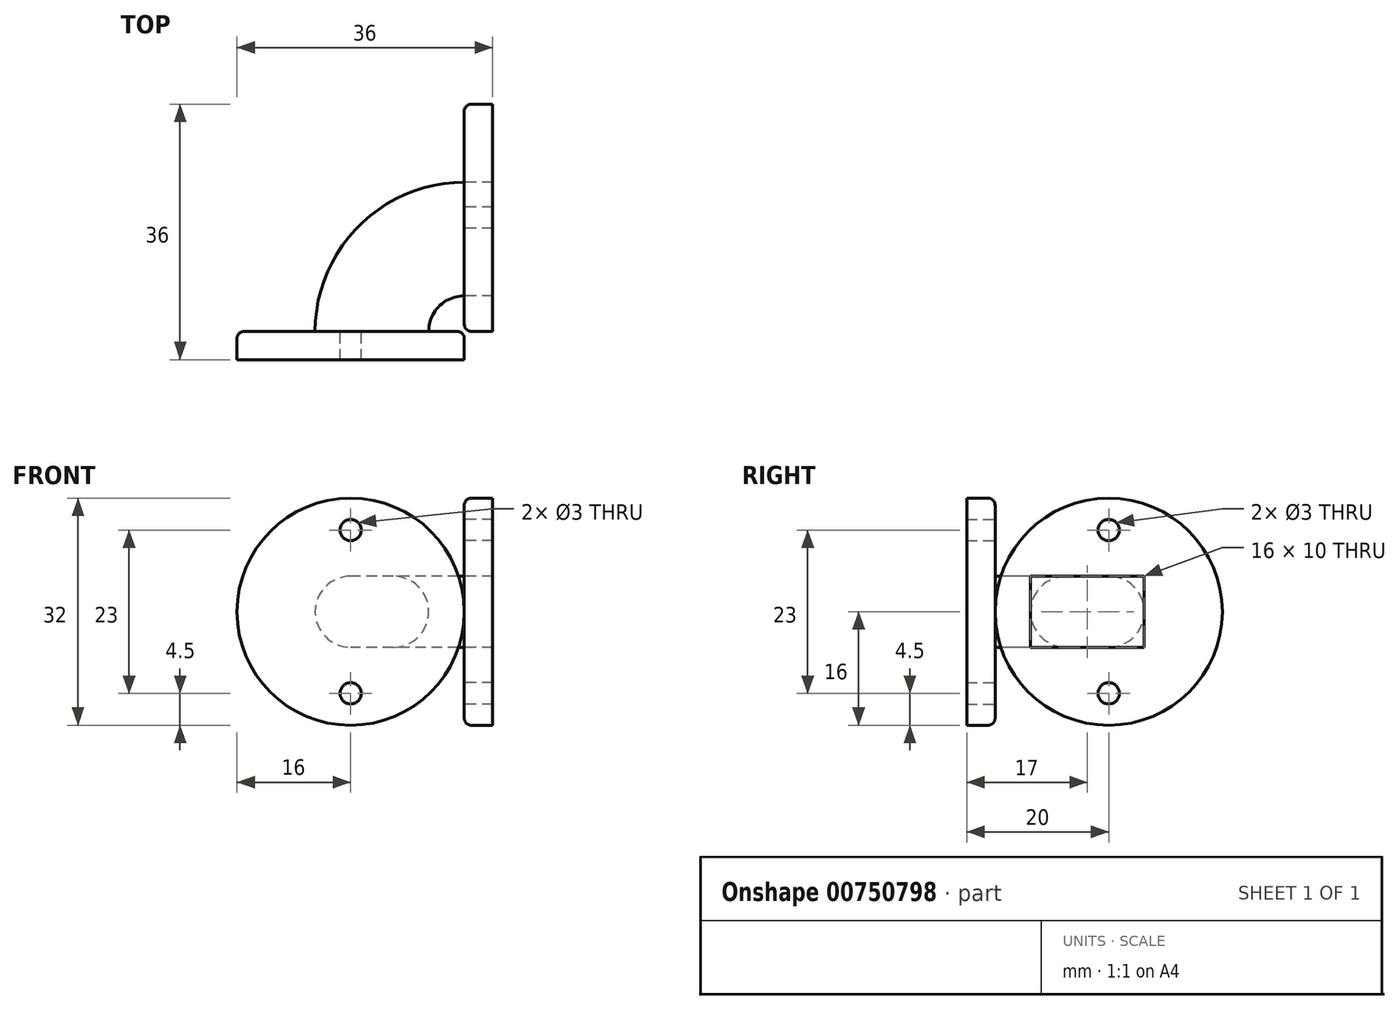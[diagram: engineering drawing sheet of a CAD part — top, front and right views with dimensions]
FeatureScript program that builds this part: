
annotation { "Feature Type Name" : "Feature", "Feature Type Description" : "" }
export const myFeature = defineFeature(function(context is Context, id is Id, definition is map)
    precondition{}
    {
        {
            var Q0;
            Q0=qCreatedBy(makeId("Front.planeOp"),FACE);
            var sketch = newSketch(context, id + "F0", { "sketchPlane" : qUnion([Q0])});
            skCircle(sketch, "E0", {"center": v(0, 0) * mm, "radius": 16 * mm});
            skCircle(sketch, "E1", {"center": v(0, -11.5) * mm, "radius": 1.5 * mm});
            skCircle(sketch, "E2", {"center": v(0, 11.5) * mm, "radius": 1.5 * mm});
            skSolve(sketch);
        }
        {
            var Q0;
            Q0=makeQuery(id+"F0.imprint","IMPRINT",FACE,{"disambiguationData":[TD([[makeQuery(id+"F0.imprint","IMPRINT",EDGE,{"derivedFrom":sQuery(id+"F0.wireOp",EDGE,"E0")}),1.0]])]});
            extrude(context, id + "F1", {"entities" : qUnion([Q0]), "depth" : 4 * mm, "offsetDistance" : 25 * mm});
        }
        {
            var Q0;
            Q0=qCreatedBy(makeId("Top.planeOp"),FACE);
            var sketch = newSketch(context, id + "F2", { "sketchPlane" : qUnion([Q0])});
            skCircle(sketch, "E3", {"center": v(16, 0) * mm, "radius": 16 * mm});
            skLineSegment(sketch, "E4", {"start": v(0, 0) * mm, "end": v(16, 0) * mm});
            skLineSegment(sketch, "E5", {"start": v(16, 0) * mm, "end": v(16, 16) * mm});
            skCircle(sketch, "E6", {"center": v(16, 0) * mm, "radius": 5 * mm});
            skCircle(sketch, "E7", {"center": v(16, 0) * mm, "radius": 21 * mm});
            skLineSegment(sketch, "E8", {"start": v(16, 16) * mm, "end": v(16, 21) * mm});
            skLineSegment(sketch, "E9", {"start": v(0, 0) * mm, "end": v(-5, 0) * mm});
            skSolve(sketch);
        }
        {
            var Q0;
            {var subQ2=sQuery(id+"F2.wireOp",EDGE,"E8");Q0=makeQuery(id+"F2.imprint","IMPRINT",FACE,{"disambiguationData":[TD([[makeQuery(id+"F2.imprint","IMPRINT",EDGE,{"derivedFrom":subQ2}),1.0]])]});}
            var Q1;
            {var subQ0=sQuery(id+"F2.wireOp",EDGE,"E4");var subQ5=sQuery(id+"F2.wireOp",EDGE,"E6");var subQ7=makeQuery(id+"F2.imprint","INTERSECT",VERTEX,{"derivedFrom":[subQ0,subQ5]});Q1=makeQuery(id+"F2.imprint","IMPRINT",FACE,{"disambiguationData":[TD([[makeQuery(id+"F2.imprint","IMPRINT",EDGE,{"disambiguationData":[TD([[subQ7,1.0]])],"derivedFrom":subQ5}),-1.0]])]});}
            extrude(context, id + "F3", {"entities" : qUnion([Q0, Q1]), "operationType" : NewBodyOperationType.ADD, "endBound" : BoundingType.SYMMETRIC, "depth" : 10 * mm, "offsetDistance" : 25 * mm});
        }
        {
            var Q0;
            Q0=makeQuery(id+"F3.opExtrude","SWEPT_FACE",FACE,{"disambiguationData":[OSD([sQuery(id+"F2.wireOp",EDGE,"E5"),sQuery(id+"F2.wireOp",EDGE,"E8")])]});
            var sketch = newSketch(context, id + "F4", { "sketchPlane" : qUnion([Q0])});
            skCircle(sketch, "E10", {"center": v(16, 0) * mm, "radius": 16 * mm});
            skCircle(sketch, "E11", {"center": v(16, -11.5) * mm, "radius": 1.5 * mm});
            skCircle(sketch, "E12", {"center": v(16, 11.5) * mm, "radius": 1.5 * mm});
            skSolve(sketch);
        }
        {
            var Q0;
            Q0=makeQuery(id+"F4.imprint","IMPRINT",FACE,{"disambiguationData":[TD([[makeQuery(id+"F4.imprint","IMPRINT",EDGE,{"derivedFrom":sQuery(id+"F4.wireOp",EDGE,"E10")}),1.0]])]});
            extrude(context, id + "F5", {"entities" : qUnion([Q0]), "operationType" : NewBodyOperationType.ADD, "depth" : 4 * mm, "offsetDistance" : 25 * mm});
        }
        {
            var Q0;
            {var subQ0=sQuery(id+"F2.wireOp",EDGE,"E8");var subQ1=sQuery(id+"F2.wireOp",EDGE,"E5");Q0=makeQuery(id+"F5.opExtrude","SWEPT_FACE",FACE,{"disambiguationData":[OSD([subQ1,subQ0]),TDD([makeQuery(id+"F4.imprint","IMPRINT",EDGE,{"derivedFrom":makeQuery(id+"F3.opExtrude","CAP_EDGE",EDGE,{"disambiguationData":[OSD([subQ1,subQ0])],"isStart":false})})])]});}
            var sketch = newSketch(context, id + "F6", { "sketchPlane" : qUnion([Q0])});
            skLineSegment(sketch, "E13.bottom", {"start": v(20, -5) * mm, "end": v(16, -5) * mm});
            skLineSegment(sketch, "E13.top", {"start": v(20, -21) * mm, "end": v(16, -21) * mm});
            skLineSegment(sketch, "E13.left", {"start": v(20, -5) * mm, "end": v(20, -21) * mm});
            skLineSegment(sketch, "E13.right", {"start": v(16, -5) * mm, "end": v(16, -21) * mm});
            skSolve(sketch);
        }
        {
            var Q0;
            Q0=makeQuery(id+"F6.imprint","IMPRINT",FACE,{"disambiguationData":[TD([[makeQuery(id+"F6.imprint","IMPRINT",EDGE,{"derivedFrom":sQuery(id+"F6.wireOp",EDGE,"E13.bottom")}),1.0]])]});
            extrude(context, id + "F7", {"entities" : qUnion([Q0]), "endBound" : BoundingType.UP_TO_NEXT, "depth" : 25 * mm, "offsetDistance" : 25 * mm});
        }
        {
            var Q0;
            Q0=makeQuery(id+"F3.opExtrude","CAP_EDGE",EDGE,{"disambiguationData":[OSD([sQuery(id+"F2.wireOp",EDGE,"E7")])],"isStart":false});
            var Q1;
            Q1=makeQuery(id+"F3.opExtrude","CAP_EDGE",EDGE,{"disambiguationData":[OSD([sQuery(id+"F2.wireOp",EDGE,"E6")])],"isStart":false});
            var Q2;
            Q2=makeQuery(id+"F3.opExtrude","CAP_EDGE",EDGE,{"disambiguationData":[OSD([sQuery(id+"F2.wireOp",EDGE,"E6")])],"isStart":true});
            var Q3;
            Q3=makeQuery(id+"F3.opExtrude","CAP_EDGE",EDGE,{"disambiguationData":[OSD([sQuery(id+"F2.wireOp",EDGE,"E7")])],"isStart":true});
            fillet(context, id + "F8", {"entities" : qUnion([Q0, Q1, Q2, Q3]), "radius" : 5 * mm, "tangentPropagation" : true, "allowEdgeOverflow" : false});
        }
        {
            var Q0;
            Q0=makeQuery(id+"F1.opExtrude","CAP_EDGE",EDGE,{"disambiguationData":[OSD([sQuery(id+"F0.wireOp",EDGE,"E0")])],"isStart":true});
            fillet(context, id + "F9", {"entities" : qUnion([Q0]), "radius" : 1 * mm, "tangentPropagation" : true, "allowEdgeOverflow" : false});
        }
        {
            var Q0;
            Q0=makeQuery(id+"F5.opExtrude","CAP_EDGE",EDGE,{"disambiguationData":[OSD([sQuery(id+"F4.wireOp",EDGE,"E10")])],"isStart":true});
            fillet(context, id + "F10", {"entities" : qUnion([Q0]), "radius" : 1 * mm, "tangentPropagation" : true, "allowEdgeOverflow" : false});
        }
    });
